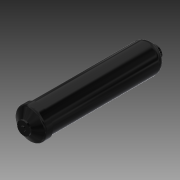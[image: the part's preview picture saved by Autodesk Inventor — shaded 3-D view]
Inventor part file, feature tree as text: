
AUTODESK INVENTOR PART (.ipt)
format: ipt  version: 2019 (Build 230136000, 136)  size: 152,576 bytes
history: native  units: in
note: dims shown in document units (in); Inventor stores cm internally (conversion verified against a paired STEP export)
features: sketch x7, extrude x4, revolve x3, fillet x2, projected_geometry x2, plane x1
ambient origin geometry x8: Origin, YZ Plane, XZ Plane, XY Plane, X Axis, Y Axis, Z Axis, Center Point
bodies: Solid1 (feature_tree)
feature tree (19):
  revolve  "Revolution1"  [1 undecoded]
  fillet  "Fillet1"  [1 undecoded]
  revolve  "Revolution2"  [1 undecoded]
  fillet  "Fillet2"  Radius=0.75in
  revolve  "Revolution3"  [1 undecoded]
  extrude  "Extrusion1"  Depth=0.144in TaperAngle=0.0deg
  extrude  "Extrusion2"  Depth=0.1in TaperAngle=0.0deg
  extrude  "Extrusion3"  [1 undecoded]
  extrude  "Extrusion4"  [1 undecoded]
  plane  "Work Plane1"
  sketch  "Sketch1"  dims[d0=1.28in d1=10.459in d2=90.0deg]
  sketch  "Sketch2"  dims[d3=0.75in d4=1.39in d5=0.75in]
  sketch  "Sketch3"  dims[d6=90.0deg d7=0.25in]
  sketch  "Sketch4"  dims[d8=90.0deg d9=0.144in d10=0.0in]
  projected_geometry  "Projected Loop1"
  sketch  "Sketch5"  dims[d11=0.322in d12=0.0in d13=0.1in d14=0.0in]
  projected_geometry  "Projected Loop2"
  sketch  "Sketch6"  dims[d15=0.1in d16=0.0in]
  sketch  "Sketch7"
note: 6 required parameter values undecoded (feature->parameter linkage not recoverable at this tier; creation-order binding heuristic only, values carry confidence <= 0.55)